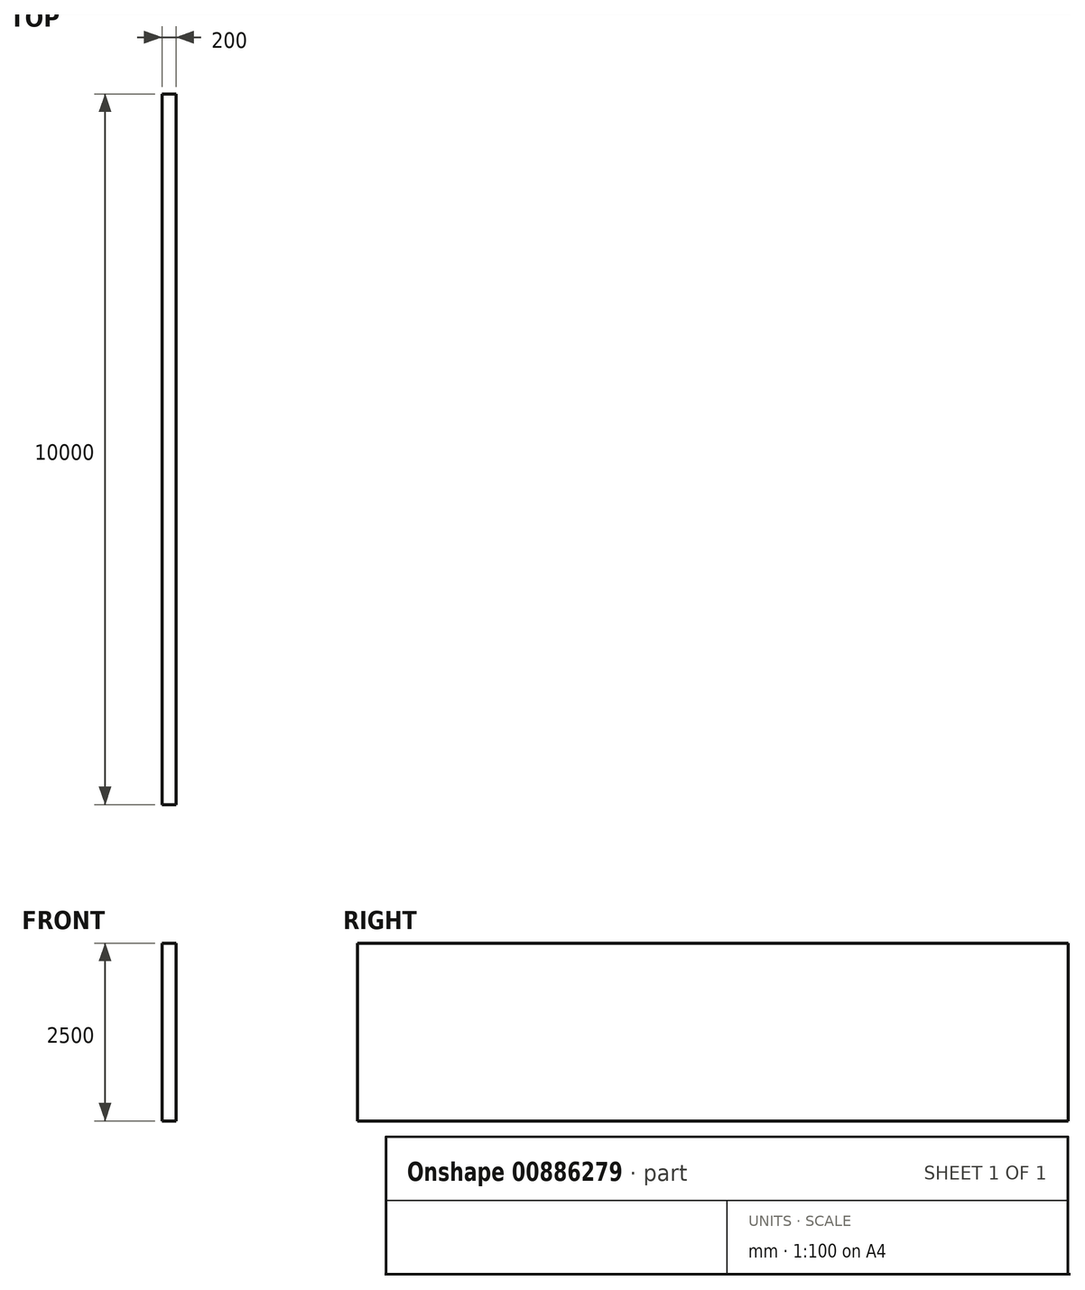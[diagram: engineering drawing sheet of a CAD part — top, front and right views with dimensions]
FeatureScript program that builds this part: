
annotation { "Feature Type Name" : "Feature", "Feature Type Description" : "" }
export const myFeature = defineFeature(function(context is Context, id is Id, definition is map)
    precondition{}
    {
        {
            var Q0;
            Q0=qCreatedBy(makeId("Top.planeOp"),FACE);
            var sketch = newSketch(context, id + "F0", { "sketchPlane" : qUnion([Q0])});
            skLineSegment(sketch, "E0.top", {"start": v(-67.35, -147.8) * mm, "end": v(132.65, -147.8) * mm});
            skLineSegment(sketch, "E0.left", {"start": v(-67.35, 9852.2) * mm, "end": v(-67.35, -147.8) * mm});
            skLineSegment(sketch, "E0.right", {"start": v(132.65, 9852.2) * mm, "end": v(132.65, -147.8) * mm});
            skLineSegment(sketch, "E1", {"start": v(-67.35, 9852.2) * mm, "end": v(132.65, 9852.2) * mm});
            skSolve(sketch);
        }
        {
            var Q0;
            Q0=makeQuery(id+"F0.imprint","IMPRINT",FACE,{"disambiguationData":[TD([[makeQuery(id+"F0.imprint","IMPRINT",EDGE,{"derivedFrom":sQuery(id+"F0.wireOp",EDGE,"E0.top")}),1.0]])]});
            extrude(context, id + "F1", {"entities" : qUnion([Q0]), "oppositeDirection" : true, "depth" : 2500 * mm, "offsetDistance" : 25 * mm});
        }
    });
